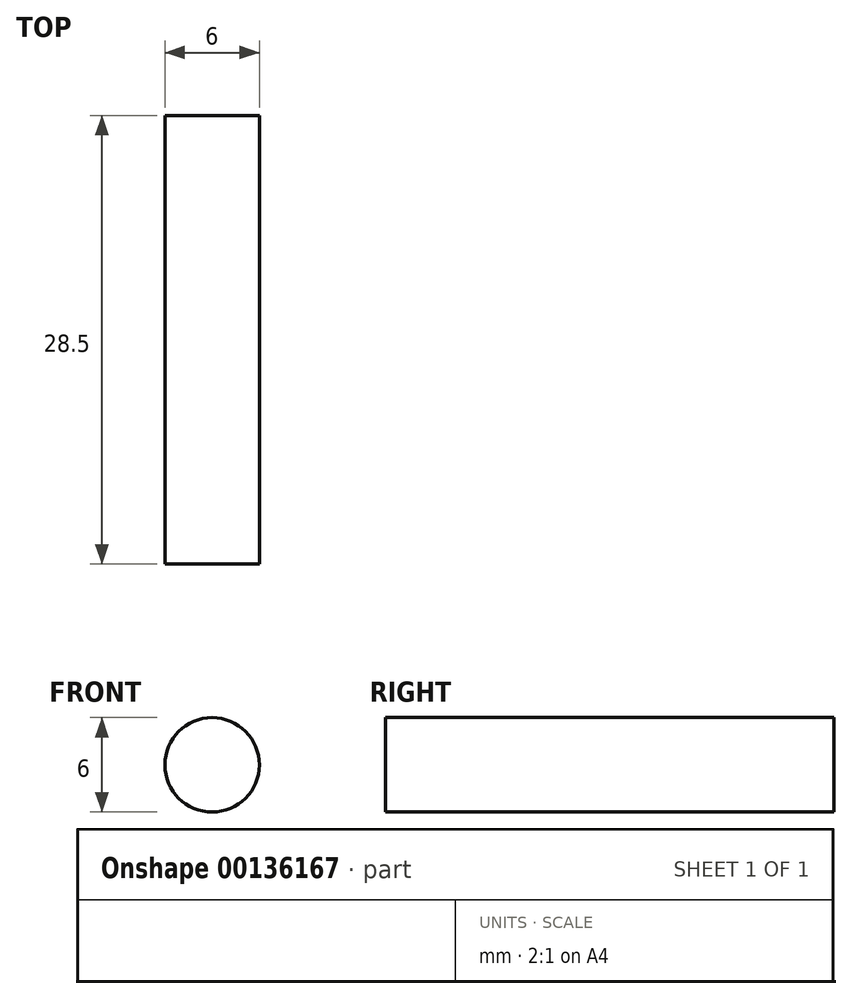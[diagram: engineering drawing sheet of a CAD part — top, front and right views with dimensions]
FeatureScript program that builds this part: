
annotation { "Feature Type Name" : "Feature", "Feature Type Description" : "" }
export const myFeature = defineFeature(function(context is Context, id is Id, definition is map)
    precondition{}
    {
        {
            var Q0;
            Q0=qCreatedBy(makeId("Front.planeOp"),FACE);
            var sketch = newSketch(context, id + "F0", { "sketchPlane" : qUnion([Q0])});
            skCircle(sketch, "E0", {"center": v(0, 0) * mm, "radius": 3 * mm});
            skSolve(sketch);
        }
        {
            var Q0;
            Q0 = qSketchRegion(id + "F0", true);
            extrude(context, id + "F1", {"entities" : qUnion([Q0]), "depth" : 28.5 * mm});
        }
    });
